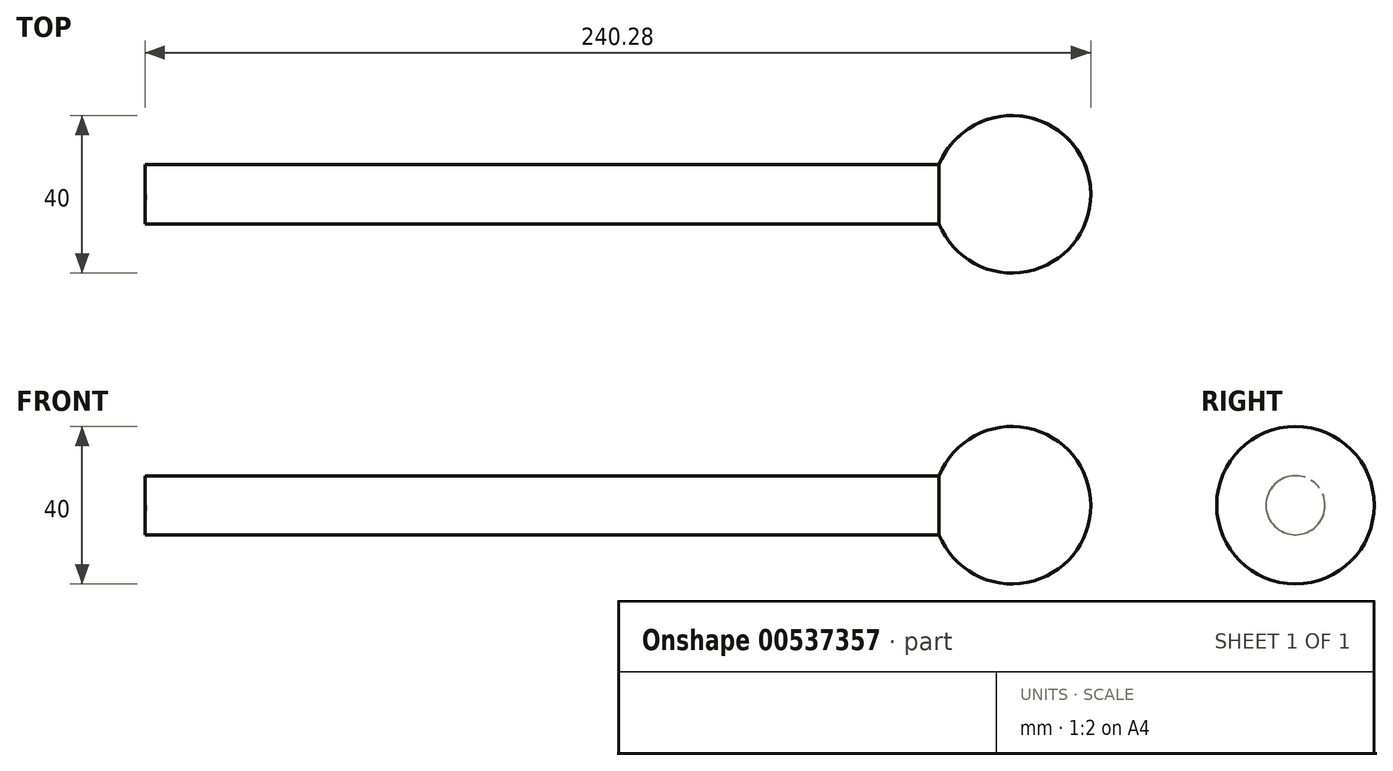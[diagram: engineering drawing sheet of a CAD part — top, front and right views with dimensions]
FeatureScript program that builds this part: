
annotation { "Feature Type Name" : "Feature", "Feature Type Description" : "" }
export const myFeature = defineFeature(function(context is Context, id is Id, definition is map)
    precondition{}
    {
        {
            var Q0;
            Q0=qCreatedBy(makeId("Top.planeOp"),FACE);
            var sketch = newSketch(context, id + "F0", { "sketchPlane" : qUnion([Q0])});
            skPoint(sketch, "E0.right.start.orphan", {"position": v(98.15, 7.36) * mm});
            skPoint(sketch, "E1.orphan", {"position": v(98.15, -7.36) * mm});
            skPoint(sketch, "E2.orphan", {"position": v(24.54, -26.86) * mm});
            skLineSegment(sketch, "E3.bottom", {"start": v(1.46, 7.5) * mm, "end": v(-200.28, 7.5) * mm});
            skLineSegment(sketch, "E3.right", {"start": v(-200.28, 7.5) * mm, "end": v(-200, 0) * mm});
            skPoint(sketch, "E3.middle", {"position": v(0, 0) * mm});
            skArc(sketch, "E4", {"start": v(40, 0) * mm, "mid": v(23.82, 19.63) * mm, "end": v(1.46, 7.5) * mm});
            skLineSegment(sketch, "E5", {"start": v(-200, 0) * mm, "end": v(200, 0) * mm, "construction": true});
            skPoint(sketch, "E6.orphan", {"position": v(-199.72, -7.5) * mm});
            skPoint(sketch, "E7.orphan", {"position": v(199.72, 7.5) * mm});
            skPoint(sketch, "E3.left.end.orphan", {"position": v(200.28, -7.5) * mm});
            skLineSegment(sketch, "E8", {"start": v(-200, 0) * mm, "end": v(40, 0) * mm});
            skSolve(sketch);
        }
        {
            var Q0;
            Q0=qSketchRegion(id+"F0",true);
            var Q1;
            Q1=sQuery(id+"F0.wireOp",EDGE,"E5");
            revolve(context, id + "F1", {"entities" : qUnion([Q0]), "axis" : qUnion([Q1]), "revolveType" : RevolveType.FULL});
        }
    });
